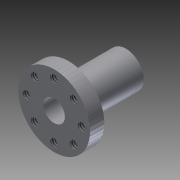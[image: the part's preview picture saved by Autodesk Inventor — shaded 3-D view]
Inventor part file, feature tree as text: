
AUTODESK INVENTOR PART (.ipt)
format: ipt  version: 2015 (Build 190159000, 159)  size: 5,733,376 bytes
history: native  units: in
note: dims shown in document units (in); Inventor stores cm internally (conversion verified against a paired STEP export)
features: thread x8, hole x8, sketch x7, other x3, extrude x2
ambient origin geometry x8: Origin, YZ Plane, XZ Plane, XY Plane, X Axis, Y Axis, Z Axis, Center Point
bodies: Body1 (feature_tree), Body2 (feature_tree), Body3 (feature_tree), Body4 (feature_tree), Body5 (feature_tree), Body6 (feature_tree), Body7 (feature_tree), Body8 (feature_tree), Body9 (feature_tree), Body10 (feature_tree), Body11 (feature_tree), Body12 (feature_tree), Body13 (feature_tree), Body14 (feature_tree), Body15 (feature_tree), Body16 (feature_tree), Body17 (feature_tree), Body18 (feature_tree), Body19 (feature_tree), Body20 (feature_tree), Body21 (feature_tree), Body22 (feature_tree), Body23 (feature_tree), Body24 (feature_tree), Body25 (feature_tree), Body26 (feature_tree), Body27 (feature_tree), Body28 (feature_tree), Body29 (feature_tree), Body30 (feature_tree), Body31 (feature_tree), Body32 (feature_tree), Body33 (feature_tree), Body34 (feature_tree), Body35 (feature_tree), Body36 (feature_tree), Body37 (feature_tree), Body38 (feature_tree), Body39 (feature_tree), Body40 (feature_tree), Body41 (feature_tree), Body42 (feature_tree), Body43 (feature_tree), Body44 (feature_tree), Body45 (feature_tree), Body46 (feature_tree), Body47 (feature_tree), Body48 (feature_tree), Body49 (feature_tree), Body50 (feature_tree), Body51 (feature_tree), Body52 (feature_tree), Body53 (feature_tree), Body54 (feature_tree), Body55 (feature_tree), Body56 (feature_tree), Body57 (feature_tree), Body58 (feature_tree), Body59 (feature_tree), Body60 (feature_tree), Body61 (feature_tree), Body62 (feature_tree), Body63 (feature_tree), Body64 (feature_tree), Body65 (feature_tree), Body66 (feature_tree), Body67 (feature_tree), Body68 (feature_tree), Body69 (feature_tree), Body70 (feature_tree), Body71 (feature_tree), Body72 (feature_tree), Body73 (feature_tree), Body74 (feature_tree), Body75 (feature_tree), Body76 (feature_tree), Body77 (feature_tree), Body78 (feature_tree), Body79 (feature_tree), Body80 (feature_tree), Body81 (feature_tree), Body82 (feature_tree), Body83 (feature_tree), Body84 (feature_tree), Body85 (feature_tree), Body86 (feature_tree), Body87 (feature_tree), Body88 (feature_tree), Body89 (feature_tree), Body90 (feature_tree), Body91 (feature_tree), Body92 (feature_tree), Body93 (feature_tree), Body94 (feature_tree), Body95 (feature_tree), Body96 (feature_tree), Body97 (feature_tree), Body98 (feature_tree), Body99 (feature_tree), Body100 (feature_tree), Body101 (feature_tree), Body102 (feature_tree), Body103 (feature_tree), Body104 (feature_tree), Body105 (feature_tree), Body106 (feature_tree), Body107 (feature_tree), Body108 (feature_tree), Body109 (feature_tree), Body110 (feature_tree), Body111 (feature_tree), Body112 (feature_tree), Body113 (feature_tree), Body114 (feature_tree), Body115 (feature_tree), Body116 (feature_tree), Body117 (feature_tree), Body118 (feature_tree), Body119 (feature_tree), Body120 (feature_tree), Body121 (feature_tree), Body122 (feature_tree), Body123 (feature_tree), Body124 (feature_tree), Body125 (feature_tree), Body126 (feature_tree), Body127 (feature_tree), Body128 (feature_tree), Body129 (feature_tree), Body130 (feature_tree), Body131 (feature_tree), Body132 (feature_tree), Body133 (feature_tree), Body134 (feature_tree), Body135 (feature_tree), Body136 (feature_tree), Body137 (feature_tree), Body138 (feature_tree), Body139 (feature_tree), Body140 (feature_tree), Body141 (feature_tree), Body142 (feature_tree), Body143 (feature_tree), Body144 (feature_tree), Body145 (feature_tree), Body146 (feature_tree), Body147 (feature_tree), Body148 (feature_tree), Body149 (feature_tree), Body150 (feature_tree), Body151 (feature_tree), Body152 (feature_tree), Body153 (feature_tree), Body154 (feature_tree), Body155 (feature_tree), Body156 (feature_tree), Body157 (feature_tree), Body158 (feature_tree), Body159 (feature_tree), Body160 (feature_tree), Body161 (feature_tree), Body162 (feature_tree), Body163 (feature_tree), Body164 (feature_tree), Body165 (feature_tree), Body166 (feature_tree), Body167 (feature_tree), Body168 (feature_tree), Body169 (feature_tree), Body170 (feature_tree), Body171 (feature_tree), Body172 (feature_tree), Body173 (feature_tree), Body174 (feature_tree), Body175 (feature_tree), Body176 (feature_tree), Body177 (feature_tree), Body178 (feature_tree), Body179 (feature_tree), Body180 (feature_tree), Body181 (feature_tree), Body182 (feature_tree), Body183 (feature_tree), Body184 (feature_tree), Body185 (feature_tree), Body186 (feature_tree), Body187 (feature_tree), Body188 (feature_tree), Body189 (feature_tree), Body190 (feature_tree), Body191 (feature_tree), Body192 (feature_tree), Body193 (feature_tree), Body194 (feature_tree), Body195 (feature_tree), Body196 (feature_tree), Body197 (feature_tree), Body198 (feature_tree), Body199 (feature_tree), Body200 (feature_tree), Body201 (feature_tree), Body202 (feature_tree), Body203 (feature_tree), Body204 (feature_tree), Body205 (feature_tree), Body206 (feature_tree), Body207 (feature_tree), Body208 (feature_tree), Body209 (feature_tree), Body210 (feature_tree), Body211 (feature_tree), Body212 (feature_tree), Body213 (feature_tree), Body214 (feature_tree), Body215 (feature_tree), Body216 (feature_tree), Body217 (feature_tree), Body218 (feature_tree), Body219 (feature_tree), Body220 (feature_tree), Body221 (feature_tree), Body222 (feature_tree), Body223 (feature_tree), Body224 (feature_tree), Body225 (feature_tree), Body226 (feature_tree), Body227 (feature_tree), Body228 (feature_tree), Body229 (feature_tree), Body230 (feature_tree), Body231 (feature_tree), Body232 (feature_tree), Body233 (feature_tree), Body234 (feature_tree), Body235 (feature_tree), Body236 (feature_tree), Body237 (feature_tree), Body238 (feature_tree), Body239 (feature_tree), Body240 (feature_tree), Body241 (feature_tree), Body242 (feature_tree), Body243 (feature_tree), Body244 (feature_tree), Body245 (feature_tree), Body246 (feature_tree), Body247 (feature_tree), Body248 (feature_tree), Body249 (feature_tree), Body250 (feature_tree), Body251 (feature_tree), Body252 (feature_tree), Body253 (feature_tree), Body254 (feature_tree), Body255 (feature_tree), Body256 (feature_tree), Body257 (feature_tree), Body258 (feature_tree), Body259 (feature_tree), Body260 (feature_tree), Body261 (feature_tree), Body262 (feature_tree), Body263 (feature_tree), Body264 (feature_tree), Body265 (feature_tree), Body266 (feature_tree), Body267 (feature_tree), Body268 (feature_tree), Body269 (feature_tree), Body270 (feature_tree), Body271 (feature_tree), Body272 (feature_tree), Body273 (feature_tree), Body274 (feature_tree), Body275 (feature_tree), Body276 (feature_tree), Body277 (feature_tree), Body278 (feature_tree), Body279 (feature_tree), Body280 (feature_tree), Body281 (feature_tree), Body282 (feature_tree), Body283 (feature_tree), Body284 (feature_tree), Body285 (feature_tree), Body286 (feature_tree), Body287 (feature_tree), Body288 (feature_tree), Body289 (feature_tree), Body290 (feature_tree), Body291 (feature_tree), Body292 (feature_tree), Body293 (feature_tree), Body294 (feature_tree), Body295 (feature_tree), Body296 (feature_tree), Body297 (feature_tree), Body298 (feature_tree), Body299 (feature_tree), Body300 (feature_tree), Body301 (feature_tree), Body302 (feature_tree), Body303 (feature_tree), Body304 (feature_tree), Body305 (feature_tree), Body306 (feature_tree), Body307 (feature_tree), Body308 (feature_tree), Body309 (feature_tree), Body310 (feature_tree), Body311 (feature_tree), Body312 (feature_tree), Body313 (feature_tree), Body314 (feature_tree), Body315 (feature_tree), Body316 (feature_tree), Body317 (feature_tree), Body318 (feature_tree), Body319 (feature_tree), Body320 (feature_tree), Body321 (feature_tree), Body322 (feature_tree), Body323 (feature_tree), Body324 (feature_tree), Body325 (feature_tree), Body326 (feature_tree), Body327 (feature_tree), Body328 (feature_tree), Body329 (feature_tree), Body330 (feature_tree), Body331 (feature_tree), Body332 (feature_tree), Body333 (feature_tree), Body334 (feature_tree), Body335 (feature_tree), Body336 (feature_tree), Body337 (feature_tree), Body338 (feature_tree), Body339 (feature_tree), Body340 (feature_tree), Body341 (feature_tree), Body342 (feature_tree), Body343 (feature_tree), Body344 (feature_tree), Body345 (feature_tree), Body346 (feature_tree), Body347 (feature_tree), Body348 (feature_tree), Body349 (feature_tree), Body350 (feature_tree), Body351 (feature_tree), Body352 (feature_tree), Body353 (feature_tree), Body354 (feature_tree), Body355 (feature_tree), Body356 (feature_tree), Body357 (feature_tree), Body358 (feature_tree), Body359 (feature_tree), Body360 (feature_tree), Body361 (feature_tree), Body362 (feature_tree), Body363 (feature_tree), Body364 (feature_tree), Body365 (feature_tree), Body366 (feature_tree), Body367 (feature_tree), Body368 (feature_tree), Body369 (feature_tree), Body370 (feature_tree), Body371 (feature_tree), Body372 (feature_tree), Body373 (feature_tree), Body374 (feature_tree), Body375 (feature_tree), Body376 (feature_tree), Body377 (feature_tree), Body378 (feature_tree), Body379 (feature_tree), Body380 (feature_tree), Body381 (feature_tree), Body382 (feature_tree), Body383 (feature_tree), Body384 (feature_tree), Body385 (feature_tree), Body386 (feature_tree), Body387 (feature_tree), Body388 (feature_tree), Body389 (feature_tree), Body390 (feature_tree), Body391 (feature_tree), Body392 (feature_tree), Body393 (feature_tree), Body394 (feature_tree), Body395 (feature_tree), Body396 (feature_tree), Body397 (feature_tree), Body398 (feature_tree), Body399 (feature_tree), Body400 (feature_tree), Body401 (feature_tree), Body402 (feature_tree), Body403 (feature_tree), Body404 (feature_tree), Body405 (feature_tree), Body406 (feature_tree), Body407 (feature_tree), Body408 (feature_tree), Body409 (feature_tree), Body410 (feature_tree), Body411 (feature_tree), Body412 (feature_tree), Body413 (feature_tree), Body414 (feature_tree), Body415 (feature_tree), Body416 (feature_tree), Body417 (feature_tree), Body418 (feature_tree), Body419 (feature_tree), Body420 (feature_tree), Body421 (feature_tree), Body422 (feature_tree), Body423 (feature_tree), Body424 (feature_tree), Body425 (feature_tree), Body426 (feature_tree), Body427 (feature_tree), Body428 (feature_tree), Body429 (feature_tree), Body430 (feature_tree), Body431 (feature_tree), Body432 (feature_tree), Body433 (feature_tree), Body434 (feature_tree), Body435 (feature_tree), Body436 (feature_tree), Body437 (feature_tree), Body438 (feature_tree), Body439 (feature_tree), Body440 (feature_tree), Body441 (feature_tree), Body442 (feature_tree), Body443 (feature_tree), Body444 (feature_tree), Body445 (feature_tree), Body446 (feature_tree), Body447 (feature_tree), Body448 (feature_tree), Body449 (feature_tree), Body450 (feature_tree), Body451 (feature_tree), Body452 (feature_tree), Body453 (feature_tree), Body454 (feature_tree), Body455 (feature_tree), Body456 (feature_tree), Body457 (feature_tree), Body458 (feature_tree), Body459 (feature_tree), Body460 (feature_tree), Body461 (feature_tree), Body462 (feature_tree), Body463 (feature_tree), Body464 (feature_tree), Body465 (feature_tree), Body466 (feature_tree), Body467 (feature_tree), Body468 (feature_tree), Body469 (feature_tree), Body470 (feature_tree), Body471 (feature_tree), Body472 (feature_tree), Body473 (feature_tree), Body474 (feature_tree), Body475 (feature_tree), Body476 (feature_tree), Body477 (feature_tree), Body478 (feature_tree), Body479 (feature_tree), Body480 (feature_tree), Body481 (feature_tree), Body482 (feature_tree), Body483 (feature_tree), Body484 (feature_tree), Body485 (feature_tree), Body486 (feature_tree), Body487 (feature_tree), Body488 (feature_tree), Body489 (feature_tree), Body490 (feature_tree), Body491 (feature_tree), Body492 (feature_tree), Body493 (feature_tree), Body494 (feature_tree), Body495 (feature_tree), Body496 (feature_tree), Body497 (feature_tree), Body498 (feature_tree), Body499 (feature_tree), Body500 (feature_tree), Body501 (feature_tree), Body502 (feature_tree), Body503 (feature_tree), Body504 (feature_tree), Body505 (feature_tree), Body506 (feature_tree), Body507 (feature_tree), Body508 (feature_tree), Body509 (feature_tree), Body510 (feature_tree), Body511 (feature_tree), Body512 (feature_tree), Body513 (feature_tree), Body514 (feature_tree), Body515 (feature_tree), Body516 (feature_tree), Body517 (feature_tree), Body518 (feature_tree), Body519 (feature_tree), Body520 (feature_tree), Body521 (feature_tree), Body522 (feature_tree), Body523 (feature_tree), Body524 (feature_tree), Body525 (feature_tree), Body526 (feature_tree), Body527 (feature_tree), Body528 (feature_tree), Body529 (feature_tree), Body530 (feature_tree), Body531 (feature_tree), Body532 (feature_tree), Body533 (feature_tree), Body534 (feature_tree), Body535 (feature_tree), Body536 (feature_tree), Body537 (feature_tree), Body538 (feature_tree), Body539 (feature_tree), Body540 (feature_tree), Body541 (feature_tree), Body542 (feature_tree), Body543 (feature_tree), Body544 (feature_tree), Body545 (feature_tree), Body546 (feature_tree), Body547 (feature_tree), Body548 (feature_tree), Body549 (feature_tree), Body550 (feature_tree), Body551 (feature_tree), Body552 (feature_tree), Body553 (feature_tree), Body554 (feature_tree), Body555 (feature_tree), Body556 (feature_tree), Body557 (feature_tree), Body558 (feature_tree), Body559 (feature_tree), Body560 (feature_tree), Body561 (feature_tree), Body562 (feature_tree), Body563 (feature_tree), Body564 (feature_tree), Body565 (feature_tree), Body566 (feature_tree), Body567 (feature_tree), Body568 (feature_tree), Body569 (feature_tree), Body570 (feature_tree), Body571 (feature_tree), Body572 (feature_tree), Body573 (feature_tree), Body574 (feature_tree), Body575 (feature_tree), Body576 (feature_tree), Body577 (feature_tree), Body578 (feature_tree), Body579 (feature_tree), Body580 (feature_tree), Body581 (feature_tree), Body582 (feature_tree), Body583 (feature_tree), Body584 (feature_tree), Body585 (feature_tree), Body586 (feature_tree), Body587 (feature_tree), Body588 (feature_tree), Body589 (feature_tree), Body590 (feature_tree), Body591 (feature_tree), Body592 (feature_tree), Body593 (feature_tree), Body594 (feature_tree), Body595 (feature_tree), Body596 (feature_tree), Body597 (feature_tree), Body598 (feature_tree), Body599 (feature_tree), Body600 (feature_tree), Body601 (feature_tree), Body602 (feature_tree), Body603 (feature_tree), Body604 (feature_tree), Body605 (feature_tree), Body606 (feature_tree), Body607 (feature_tree), Body608 (feature_tree), Body609 (feature_tree), Body610 (feature_tree), Body611 (feature_tree), Body612 (feature_tree), Body613 (feature_tree), Body614 (feature_tree), Body615 (feature_tree), Body616 (feature_tree), Body617 (feature_tree), Body618 (feature_tree), Body619 (feature_tree), Body620 (feature_tree), Body621 (feature_tree), Body622 (feature_tree), Body623 (feature_tree), Body624 (feature_tree), Body625 (feature_tree), Body626 (feature_tree), Body627 (feature_tree), Body628 (feature_tree), Body629 (feature_tree), Body630 (feature_tree), Body631 (feature_tree), Body632 (feature_tree), Body633 (feature_tree), Body634 (feature_tree), Body635 (feature_tree), Body636 (feature_tree), Body637 (feature_tree), Body638 (feature_tree), Body639 (feature_tree), Body640 (feature_tree), Body641 (feature_tree), Body642 (feature_tree), Body643 (feature_tree), Body644 (feature_tree), Body645 (feature_tree), Body646 (feature_tree), Body647 (feature_tree), Body648 (feature_tree), Body649 (feature_tree), Body650 (feature_tree), Body651 (feature_tree), Body652 (feature_tree), Body653 (feature_tree), Body654 (feature_tree), Body655 (feature_tree), Body656 (feature_tree), Body657 (feature_tree), Body658 (feature_tree), Body659 (feature_tree), Body660 (feature_tree), Body661 (feature_tree), Body662 (feature_tree), Body663 (feature_tree), Body664 (feature_tree), Body665 (feature_tree), Body666 (feature_tree), Body667 (feature_tree), Body668 (feature_tree), Body669 (feature_tree), Body670 (feature_tree), Body671 (feature_tree), Body672 (feature_tree), Body673 (feature_tree), Body674 (feature_tree), Body675 (feature_tree), Body676 (feature_tree), Body677 (feature_tree), Body678 (feature_tree), Body679 (feature_tree), Body680 (feature_tree), Body681 (feature_tree), Body682 (feature_tree), Body683 (feature_tree), Body684 (feature_tree), Body685 (feature_tree), Body686 (feature_tree), Body687 (feature_tree), Body688 (feature_tree), Body689 (feature_tree), Body690 (feature_tree), Body691 (feature_tree), Body692 (feature_tree), Body693 (feature_tree), Body694 (feature_tree), Body695 (feature_tree), Body696 (feature_tree), Body697 (feature_tree), Body698 (feature_tree), Body699 (feature_tree), Body700 (feature_tree), Body701 (feature_tree), Body702 (feature_tree), Body703 (feature_tree), Body704 (feature_tree), Body705 (feature_tree), Body706 (feature_tree), Body707 (feature_tree), Body708 (feature_tree), Body709 (feature_tree), Body710 (feature_tree), Body711 (feature_tree), Body712 (feature_tree), Body713 (feature_tree), Body714 (feature_tree), Body715 (feature_tree), Body716 (feature_tree), Body717 (feature_tree), Body718 (feature_tree), Body719 (feature_tree), Body720 (feature_tree), Body721 (feature_tree), Body722 (feature_tree), Body723 (feature_tree), Body724 (feature_tree), Body725 (feature_tree), Body726 (feature_tree), Body727 (feature_tree), Body728 (feature_tree), Body729 (feature_tree), Body730 (feature_tree), Body731 (feature_tree), Body732 (feature_tree), Body733 (feature_tree), Body734 (feature_tree), Body735 (feature_tree), Body736 (feature_tree), Body737 (feature_tree), Body738 (feature_tree), Body739 (feature_tree), Body740 (feature_tree), Body741 (feature_tree), Body742 (feature_tree), Body743 (feature_tree), Body744 (feature_tree), Body745 (feature_tree), Body746 (feature_tree), Body747 (feature_tree), Body748 (feature_tree), Body749 (feature_tree), Body750 (feature_tree), Body751 (feature_tree), Body752 (feature_tree), Body753 (feature_tree), Body754 (feature_tree), Body755 (feature_tree), Body756 (feature_tree), Body757 (feature_tree), Body758 (feature_tree), Body759 (feature_tree), Body760 (feature_tree), Body761 (feature_tree), Body762 (feature_tree), Body763 (feature_tree), Body764 (feature_tree), Body765 (feature_tree), Body766 (feature_tree), Body767 (feature_tree), Body768 (feature_tree), Body769 (feature_tree), Body770 (feature_tree), Body771 (feature_tree), Body772 (feature_tree), Body773 (feature_tree), Body774 (feature_tree), Body775 (feature_tree), Body776 (feature_tree), Body777 (feature_tree), Body778 (feature_tree), Body779 (feature_tree), Body780 (feature_tree), Body781 (feature_tree), Body782 (feature_tree), Body783 (feature_tree), Body784 (feature_tree), Body785 (feature_tree), Body786 (feature_tree), Body787 (feature_tree), Body788 (feature_tree), Body789 (feature_tree), Body790 (feature_tree), Body791 (feature_tree), Body792 (feature_tree), Body793 (feature_tree), Body794 (feature_tree), Body795 (feature_tree), Body796 (feature_tree), Body797 (feature_tree), Body798 (feature_tree), Body799 (feature_tree), Body800 (feature_tree), Body801 (feature_tree), Body802 (feature_tree), Body803 (feature_tree), Body804 (feature_tree), Body805 (feature_tree), Body806 (feature_tree), Body807 (feature_tree), Body808 (feature_tree), Body809 (feature_tree), Body810 (feature_tree), Body811 (feature_tree), Body812 (feature_tree), Body813 (feature_tree), Body814 (feature_tree), Body815 (feature_tree), Body816 (feature_tree), Body817 (feature_tree), Body818 (feature_tree), Body819 (feature_tree), Body820 (feature_tree), Body821 (feature_tree), Body822 (feature_tree), Body823 (feature_tree), Body824 (feature_tree), Body825 (feature_tree), Body826 (feature_tree), Body827 (feature_tree), Body828 (feature_tree), Body829 (feature_tree), Body830 (feature_tree), Body831 (feature_tree), Body832 (feature_tree), Body833 (feature_tree), Body834 (feature_tree), Body835 (feature_tree), Body836 (feature_tree), Body837 (feature_tree), Body838 (feature_tree), Body839 (feature_tree), Body840 (feature_tree), Body841 (feature_tree), Body842 (feature_tree), Body843 (feature_tree), Body844 (feature_tree), Body845 (feature_tree), Body846 (feature_tree), Body847 (feature_tree), Body848 (feature_tree), Body849 (feature_tree), Body850 (feature_tree), Body851 (feature_tree), Body852 (feature_tree), Body853 (feature_tree), Body854 (feature_tree), Body855 (feature_tree), Body856 (feature_tree), Body857 (feature_tree), Body858 (feature_tree), Body859 (feature_tree), Body860 (feature_tree), Body861 (feature_tree), Body862 (feature_tree), Body863 (feature_tree), Body864 (feature_tree), Body865 (feature_tree), Body866 (feature_tree), Body867 (feature_tree), Body868 (feature_tree), Body869 (feature_tree), Body870 (feature_tree), Body871 (feature_tree), Body872 (feature_tree), Body873 (feature_tree), Body874 (feature_tree), Body875 (feature_tree), Body876 (feature_tree), Body877 (feature_tree), Body878 (feature_tree), Body879 (feature_tree), Body880 (feature_tree), Body881 (feature_tree), Body882 (feature_tree), Body883 (feature_tree), Body884 (feature_tree), Body885 (feature_tree), Body886 (feature_tree), Body887 (feature_tree), Body888 (feature_tree), Body889 (feature_tree), Body890 (feature_tree), Body891 (feature_tree), Body892 (feature_tree), Body893 (feature_tree), Body894 (feature_tree), Body895 (feature_tree), Body896 (feature_tree), Body897 (feature_tree), Body898 (feature_tree), Body899 (feature_tree), Body900 (feature_tree), Body901 (feature_tree), Body902 (feature_tree), Body903 (feature_tree), Body904 (feature_tree), Body905 (feature_tree), Body906 (feature_tree), Body907 (feature_tree), Body908 (feature_tree), Body909 (feature_tree), Body910 (feature_tree), Body911 (feature_tree), Body912 (feature_tree), Body913 (feature_tree), Body914 (feature_tree), Body915 (feature_tree), Body916 (feature_tree), Body917 (feature_tree), Body918 (feature_tree), Body919 (feature_tree), Body920 (feature_tree), Body921 (feature_tree), Body922 (feature_tree), Body923 (feature_tree), Body924 (feature_tree), Body925 (feature_tree), Body926 (feature_tree), Body927 (feature_tree), Body928 (feature_tree), Body929 (feature_tree), Body930 (feature_tree), Body931 (feature_tree), Body932 (feature_tree), Body933 (feature_tree), Body934 (feature_tree), Body935 (feature_tree), Body936 (feature_tree), Body937 (feature_tree), Body938 (feature_tree), Body939 (feature_tree), Body940 (feature_tree), Body941 (feature_tree), Body942 (feature_tree), Body943 (feature_tree), Body944 (feature_tree), Body945 (feature_tree), Body946 (feature_tree), Body947 (feature_tree), Body948 (feature_tree), Body949 (feature_tree), Body950 (feature_tree), Body951 (feature_tree), Body952 (feature_tree), Body953 (feature_tree), Body954 (feature_tree), Body955 (feature_tree), Body956 (feature_tree), Body957 (feature_tree), Body958 (feature_tree), Body959 (feature_tree), Body960 (feature_tree), Body961 (feature_tree), Body962 (feature_tree), Body963 (feature_tree), Body964 (feature_tree), Body965 (feature_tree), Body966 (feature_tree), Body967 (feature_tree), Body968 (feature_tree), Body969 (feature_tree), Body970 (feature_tree), Body971 (feature_tree), Body972 (feature_tree), Body973 (feature_tree), Body974 (feature_tree), Body975 (feature_tree), Body976 (feature_tree), Body977 (feature_tree), Body978 (feature_tree), Body979 (feature_tree), Body980 (feature_tree), Body981 (feature_tree), Body982 (feature_tree), Body983 (feature_tree), Body984 (feature_tree), Body985 (feature_tree), Body986 (feature_tree), Body987 (feature_tree), Body988 (feature_tree), Body989 (feature_tree), Body990 (feature_tree), Body991 (feature_tree), Body992 (feature_tree), Body993 (feature_tree), Body994 (feature_tree), Body995 (feature_tree), Body996 (feature_tree), Body997 (feature_tree), Body998 (feature_tree), Body999 (feature_tree), Body1000 (feature_tree), Body1001 (feature_tree), Body1002 (feature_tree), Body1003 (feature_tree), Body1004 (feature_tree), Body1005 (feature_tree), Body1006 (feature_tree), Body1007 (feature_tree), Body1008 (feature_tree), Body1009 (feature_tree), Body1010 (feature_tree), Body1011 (feature_tree), Body1012 (feature_tree), Body1013 (feature_tree), Body1014 (feature_tree), Body1015 (feature_tree), Body1016 (feature_tree), Body1017 (feature_tree), Body1018 (feature_tree), Body1019 (feature_tree), Body1020 (feature_tree), Body1021 (feature_tree), Body1022 (feature_tree), Body1023 (feature_tree), Body1024 (feature_tree), Body1025 (feature_tree), Body1026 (feature_tree), Body1027 (feature_tree), Body1028 (feature_tree), Body1029 (feature_tree), Body1030 (feature_tree), Body1031 (feature_tree), Body1032 (feature_tree), Body1033 (feature_tree), Body1034 (feature_tree), Body1035 (feature_tree), Body1036 (feature_tree), Body1037 (feature_tree), Body1038 (feature_tree), Body1039 (feature_tree), Body1040 (feature_tree), Body1041 (feature_tree), Body1042 (feature_tree), Body1043 (feature_tree), Body1044 (feature_tree), Body1045 (feature_tree), Body1046 (feature_tree), Body1047 (feature_tree), Body1048 (feature_tree), Body1049 (feature_tree), Body1050 (feature_tree), Body1051 (feature_tree), Body1052 (feature_tree), Body1053 (feature_tree), Body1054 (feature_tree), Body1055 (feature_tree), Body1056 (feature_tree), Body1057 (feature_tree), Body1058 (feature_tree), Body1059 (feature_tree), Body1060 (feature_tree), Body1061 (feature_tree), Body1062 (feature_tree), Body1063 (feature_tree), Body1064 (feature_tree), Body1065 (feature_tree), Body1066 (feature_tree), Body1067 (feature_tree), Body1068 (feature_tree), Body1069 (feature_tree), Body1070 (feature_tree), Body1071 (feature_tree), Body1072 (feature_tree), Body1073 (feature_tree), Body1074 (feature_tree), Body1075 (feature_tree), Body1076 (feature_tree), Body1077 (feature_tree), Body1078 (feature_tree), Body1079 (feature_tree), Body1080 (feature_tree), Body1081 (feature_tree), Body1082 (feature_tree), Body1083 (feature_tree), Body1084 (feature_tree), Body1085 (feature_tree), Body1086 (feature_tree), Body1087 (feature_tree), Body1088 (feature_tree), Body1089 (feature_tree), Body1090 (feature_tree), Body1091 (feature_tree), Body1092 (feature_tree), Body1093 (feature_tree), Body1094 (feature_tree), Body1095 (feature_tree), Body1096 (feature_tree), Body1097 (feature_tree), Body1098 (feature_tree), Body1099 (feature_tree), Body1100 (feature_tree), Body1101 (feature_tree), Body1102 (feature_tree), Body1103 (feature_tree), Body1104 (feature_tree), Body1105 (feature_tree), Body1106 (feature_tree), Body1107 (feature_tree), Body1108 (feature_tree), Body1109 (feature_tree), Body1110 (feature_tree), Body1111 (feature_tree), Body1112 (feature_tree), Body1113 (feature_tree), Body1114 (feature_tree), Body1115 (feature_tree), Body1116 (feature_tree), Body1117 (feature_tree), Body1118 (feature_tree), Body1119 (feature_tree), Body1120 (feature_tree), Body1121 (feature_tree), Body1122 (feature_tree), Body1123 (feature_tree), Body1124 (feature_tree), Body1125 (feature_tree), Body1126 (feature_tree), Body1127 (feature_tree), Body1128 (feature_tree), Body1129 (feature_tree), Body1130 (feature_tree), Body1131 (feature_tree), Body1132 (feature_tree), Body1133 (feature_tree), Body1134 (feature_tree), Body1135 (feature_tree), Body1136 (feature_tree), Body1137 (feature_tree), Body1138 (feature_tree), Body1139 (feature_tree), Body1140 (feature_tree), Body1141 (feature_tree), Body1142 (feature_tree), Body1143 (feature_tree), Body1144 (feature_tree), Body1145 (feature_tree), Body1146 (feature_tree), Body1147 (feature_tree), Body1148 (feature_tree), Body1149 (feature_tree), Body1150 (feature_tree), Body1151 (feature_tree), Body1152 (feature_tree), Body1153 (feature_tree), Body1154 (feature_tree), Body1155 (feature_tree), Body1156 (feature_tree), Body1157 (feature_tree), Body1158 (feature_tree), Body1159 (feature_tree), Body1160 (feature_tree), Body1161 (feature_tree), Body1162 (feature_tree), Body1163 (feature_tree), Body1164 (feature_tree), Body1165 (feature_tree), Body1166 (feature_tree), Body1167 (feature_tree), Body1168 (feature_tree), Body1169 (feature_tree), Body1170 (feature_tree), Body1171 (feature_tree), Body1172 (feature_tree), Body1173 (feature_tree), Body1174 (feature_tree), Body1175 (feature_tree), Body1176 (feature_tree), Body1177 (feature_tree), Body1178 (feature_tree), Body1179 (feature_tree), Body1180 (feature_tree), Body1181 (feature_tree), Body1182 (feature_tree), Body1183 (feature_tree), Body1184 (feature_tree), Body1185 (feature_tree), Body1186 (feature_tree), Body1187 (feature_tree), Body1188 (feature_tree), Body1189 (feature_tree), Body1190 (feature_tree), Body1191 (feature_tree), Body1192 (feature_tree), Body1193 (feature_tree), Body1194 (feature_tree), Body1195 (feature_tree), Body1196 (feature_tree), Body1197 (feature_tree), Body1198 (feature_tree), Body1199 (feature_tree), Body1200 (feature_tree), Body1201 (feature_tree), Body1202 (feature_tree), Body1203 (feature_tree), Body1204 (feature_tree), Body1205 (feature_tree), Body1206 (feature_tree), Body1207 (feature_tree), Body1208 (feature_tree), Body1209 (feature_tree), Body1210 (feature_tree), Body1211 (feature_tree), Body1212 (feature_tree), Body1213 (feature_tree), Body1214 (feature_tree), Body1215 (feature_tree), Body1216 (feature_tree), Body1217 (feature_tree), Body1218 (feature_tree), Body1219 (feature_tree), Body1220 (feature_tree), Body1221 (feature_tree), Body1222 (feature_tree), Body1223 (feature_tree), Body1224 (feature_tree), Body1225 (feature_tree), Body1226 (feature_tree), Body1227 (feature_tree), Body1228 (feature_tree), Body1229 (feature_tree), Body1230 (feature_tree), Body1231 (feature_tree), Body1232 (feature_tree), Body1233 (feature_tree), Body1234 (feature_tree), Body1235 (feature_tree), Body1236 (feature_tree), Body1237 (feature_tree), Body1238 (feature_tree), Body1239 (feature_tree), Body1240 (feature_tree), Body1241 (feature_tree), Body1242 (feature_tree), Body1243 (feature_tree), Body1244 (feature_tree), Body1245 (feature_tree), Body1246 (feature_tree), Body1247 (feature_tree), Body1248 (feature_tree), Body1249 (feature_tree), Body1250 (feature_tree), Body1251 (feature_tree), Body1252 (feature_tree), Body1253 (feature_tree), Body1254 (feature_tree)
feature tree (28):
  other  "525122.dwg1"
  extrude  "Extrusion2"  TaperAngle=0.0deg  [1 undecoded]
  extrude  "Extrusion3"  Depth=1.0in
  sketch  "Sketch7"  dims[d24=1.0in d25=0.0in d26=1.0in d27=0.0in]
  thread  "Thread1"  [1 undecoded]
  thread  "Thread2"  [1 undecoded]
  thread  "Thread3"  [1 undecoded]
  thread  "Thread4"  [1 undecoded]
  thread  "Thread5"  [1 undecoded]
  thread  "Thread6"  [1 undecoded]
  thread  "Thread7"  [1 undecoded]
  thread  "Thread8"  [1 undecoded]
  hole  "Hole2"  [1 undecoded]
  hole  "Hole4"  [1 undecoded]
  hole  "Hole6"  [1 undecoded]
  hole  "Hole8"  [1 undecoded]
  other  "3D TITLE_BLOCK"
  sketch  "Sketch4"  dims[d2=1.0in d5=0.0in]
  sketch  "Sketch6"  dims[d6=0.0in d8=0.1065in d9=3.1496in d11=360.0deg d13=0.77in d14=0.3in d15=1.0in d16=0.0in d17=0.5in d18=1.0in d19=0.0in d20=1.0in d21=0.0in d22=1.0in d23=0.0in]
  sketch  "Sketch8"  dims[d28=1.0in d29=0.0in d30=1.0in d31=0.0in]
  hole  "Hole1"  [1 undecoded]
  sketch  "Sketch9"  dims[d32=1.0in d33=0.0in d34=1.0in d35=0.0in]
  hole  "Hole3"  [1 undecoded]
  sketch  "Sketch10"  dims[d36=0.104in d37=0.319in d38=0.375in d39=0.25in d40=0.5635in d41=0.388in d42=120.0deg]
  hole  "Hole5"  [1 undecoded]
  sketch  "Sketch11"  dims[d43=0.104in d44=0.319in d45=0.375in d46=0.25in d47=0.5635in d48=0.388in d49=120.0deg d50=0.104in d51=0.319in d52=0.375in d53=0.25in d54=0.5635in d55=0.388in d56=120.0deg d57=0.104in d58=0.319in d59=0.375in d60=0.25in d61=0.5635in d62=0.388in d63=120.0deg]
  hole  "Hole7"  [1 undecoded]
  other  "Srf1"
note: 17 required parameter values undecoded (feature->parameter linkage not recoverable at this tier; creation-order binding heuristic only, values carry confidence <= 0.55)
